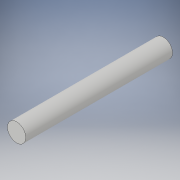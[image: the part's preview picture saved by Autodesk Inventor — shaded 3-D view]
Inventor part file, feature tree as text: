
AUTODESK INVENTOR PART (.ipt)
format: ipt  version: 2019 (Build 230136000, 136)  size: 89,088 bytes
history: native  units: in
note: dims shown in document units (in); Inventor stores cm internally (conversion verified against a paired STEP export)
features: extrude x1, sketch x1
ambient origin geometry x8: Origin, YZ Plane, XZ Plane, XY Plane, X Axis, Y Axis, Z Axis, Center Point
bodies: Solid1 (feature_tree)
feature tree (2):
  extrude  "Extrusion1"  [1 undecoded]
  sketch  "Sketch1"  dims[d1=2.0in d2=0.0in]
note: 1 required parameter value undecoded (feature->parameter linkage not recoverable at this tier; creation-order binding heuristic only, values carry confidence <= 0.55)
